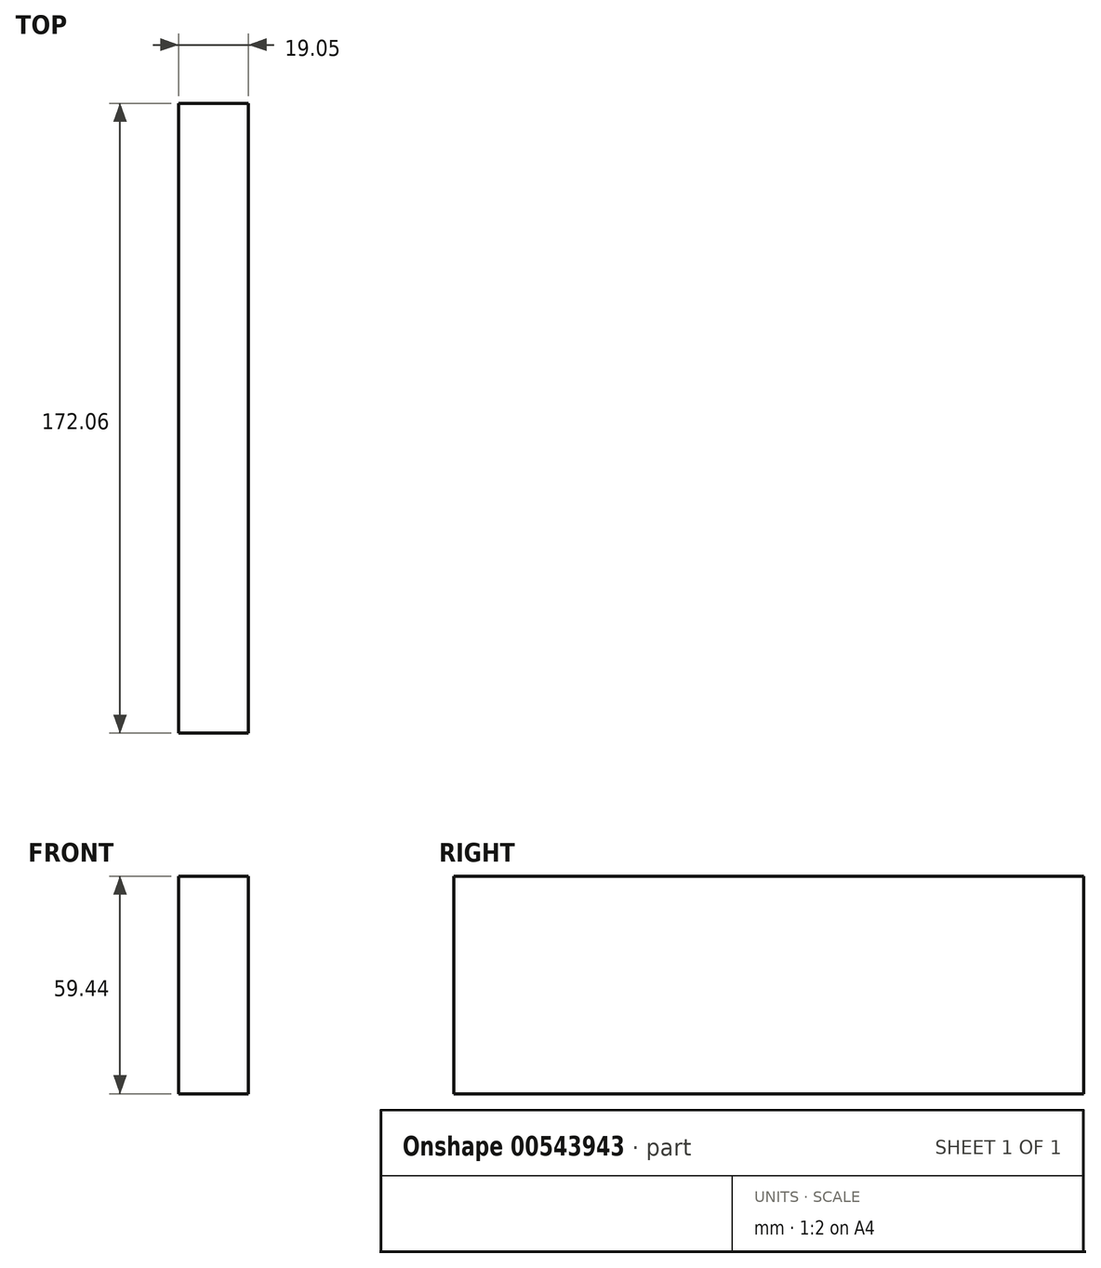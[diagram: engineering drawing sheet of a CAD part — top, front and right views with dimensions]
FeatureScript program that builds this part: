
annotation { "Feature Type Name" : "Feature", "Feature Type Description" : "" }
export const myFeature = defineFeature(function(context is Context, id is Id, definition is map)
    precondition{}
    {
        {
            var Q0;
            Q0=qCreatedBy(makeId("Right.planeOp"),FACE);
            var sketch = newSketch(context, id + "F0", { "sketchPlane" : qUnion([Q0])});
            skLineSegment(sketch, "E0.bottom", {"start": v(-104.34, 36.62) * mm, "end": v(67.72, 36.62) * mm});
            skLineSegment(sketch, "E0.top", {"start": v(-104.34, -22.82) * mm, "end": v(67.72, -22.82) * mm});
            skLineSegment(sketch, "E0.left", {"start": v(-104.34, 36.62) * mm, "end": v(-104.34, -22.82) * mm});
            skLineSegment(sketch, "E0.right", {"start": v(67.72, 36.62) * mm, "end": v(67.72, -22.82) * mm});
            skSolve(sketch);
        }
        {
            var Q0;
            Q0 = qSketchRegion(id + "F0", true);
            extrude(context, id + "F1", {"entities" : qUnion([Q0]), "depth" : 19.05 * mm, "offsetDistance" : 25.4 * mm});
        }
    });
